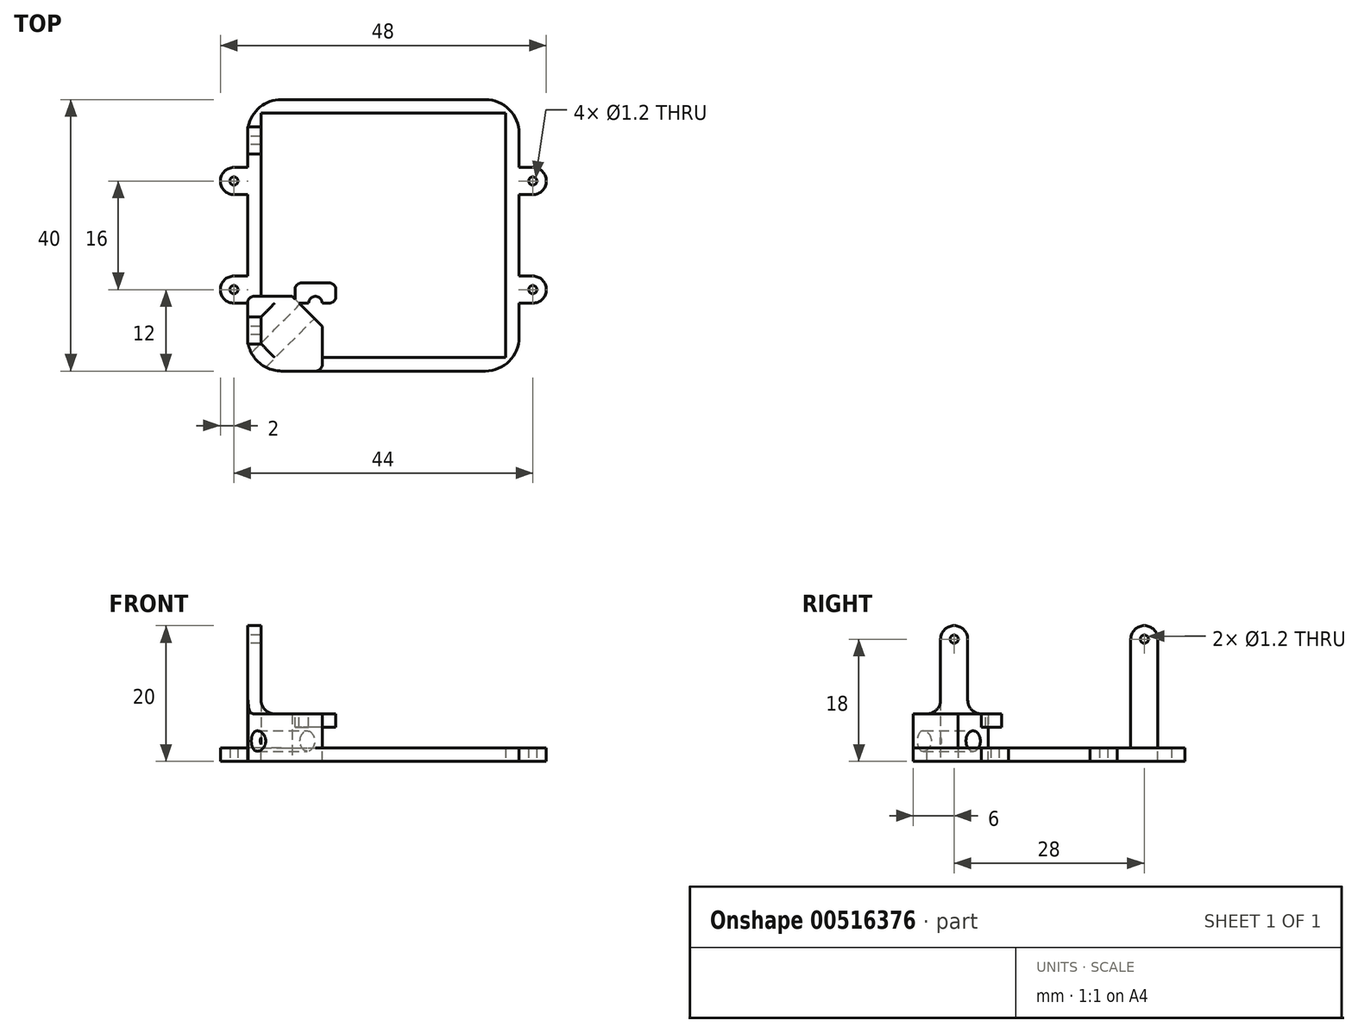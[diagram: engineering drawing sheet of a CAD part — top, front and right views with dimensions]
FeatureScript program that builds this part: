
annotation { "Feature Type Name" : "Feature", "Feature Type Description" : "" }
export const myFeature = defineFeature(function(context is Context, id is Id, definition is map)
    precondition{}
    {
        {
            var Q0;
            Q0=qCreatedBy(makeId("Top.planeOp"),FACE);
            var sketch = newSketch(context, id + "F0", { "sketchPlane" : qUnion([Q0])});
            skLineSegment(sketch, "E0.bottom", {"start": v(-10, 10) * mm, "end": v(10, 10) * mm, "construction": true});
            skLineSegment(sketch, "E0.top", {"start": v(-10, -10) * mm, "end": v(10, -10) * mm, "construction": true});
            skLineSegment(sketch, "E0.left", {"start": v(-10, 10) * mm, "end": v(-10, -10) * mm, "construction": true});
            skLineSegment(sketch, "E0.right", {"start": v(10, 10) * mm, "end": v(10, -10) * mm, "construction": true});
            skPoint(sketch, "E0.middle", {"position": v(0, 0) * mm});
            skCircle(sketch, "E1", {"center": v(-10, 10) * mm, "radius": 1 * mm});
            skCircle(sketch, "E2", {"center": v(-10, -10) * mm, "radius": 1 * mm});
            skCircle(sketch, "E3", {"center": v(10, -10) * mm, "radius": 1 * mm});
            skCircle(sketch, "E4", {"center": v(10, 10) * mm, "radius": 1 * mm});
            skLineSegment(sketch, "E5.bottom", {"start": v(-22, 8) * mm, "end": v(22, 8) * mm, "construction": true});
            skLineSegment(sketch, "E5.top", {"start": v(-22, -8) * mm, "end": v(22, -8) * mm, "construction": true});
            skLineSegment(sketch, "E5.left", {"start": v(-22, 8) * mm, "end": v(-22, -8) * mm, "construction": true});
            skLineSegment(sketch, "E5.right", {"start": v(22, 8) * mm, "end": v(22, -8) * mm, "construction": true});
            skCircle(sketch, "E6", {"center": v(-22, 8) * mm, "radius": 0.6 * mm});
            skCircle(sketch, "E7", {"center": v(22, 8) * mm, "radius": 0.6 * mm});
            skCircle(sketch, "E8", {"center": v(22, -8) * mm, "radius": 0.6 * mm});
            skCircle(sketch, "E9", {"center": v(-22, -8) * mm, "radius": 0.6 * mm});
            skLineSegment(sketch, "E10.bottom", {"start": v(-18, 18) * mm, "end": v(18, 18) * mm});
            skLineSegment(sketch, "E10.top", {"start": v(-18, -18) * mm, "end": v(18, -18) * mm});
            skLineSegment(sketch, "E10.left", {"start": v(-18, 18) * mm, "end": v(-18, -18) * mm});
            skLineSegment(sketch, "E10.right", {"start": v(18, 18) * mm, "end": v(18, -18) * mm});
            skLineSegment(sketch, "E11.bottom", {"start": v(-20, 20) * mm, "end": v(20, 20) * mm});
            skLineSegment(sketch, "E11.top", {"start": v(-20, -20) * mm, "end": v(20, -20) * mm});
            skLineSegment(sketch, "E11.left", {"start": v(-20, 20) * mm, "end": v(-20, -20) * mm});
            skLineSegment(sketch, "E11.right", {"start": v(20, 20) * mm, "end": v(20, -20) * mm});
            skArc(sketch, "E12", {"start": v(-22, 10) * mm, "mid": v(-24, 8) * mm, "end": v(-22, 6) * mm});
            skLineSegment(sketch, "E13.bottom", {"start": v(-22, 10) * mm, "end": v(22, 10) * mm});
            skLineSegment(sketch, "E13.top", {"start": v(-22, 6) * mm, "end": v(22, 6) * mm});
            skLineSegment(sketch, "E13.left", {"start": v(-22, 10) * mm, "end": v(-22, 6) * mm});
            skLineSegment(sketch, "E13.right", {"start": v(22, 10) * mm, "end": v(22, 6) * mm});
            skArc(sketch, "E14", {"start": v(22, 10) * mm, "mid": v(24, 8) * mm, "end": v(22, 6) * mm});
            skLineSegment(sketch, "E15.bottom", {"start": v(-22, -6) * mm, "end": v(22, -6) * mm});
            skLineSegment(sketch, "E15.top", {"start": v(-22, -10) * mm, "end": v(22, -10) * mm});
            skLineSegment(sketch, "E15.left", {"start": v(-22, -6) * mm, "end": v(-22, -10) * mm});
            skLineSegment(sketch, "E15.right", {"start": v(22, -6) * mm, "end": v(22, -10) * mm});
            skArc(sketch, "E16", {"start": v(-22, -6) * mm, "mid": v(-24, -8) * mm, "end": v(-22, -10) * mm});
            skArc(sketch, "E17", {"start": v(22, -6) * mm, "mid": v(24, -8) * mm, "end": v(22, -10) * mm});
            skLineSegment(sketch, "E18.bottom", {"start": v(-13.5, 13.5) * mm, "end": v(13.5, 13.5) * mm, "construction": true});
            skLineSegment(sketch, "E18.top", {"start": v(-13.5, -13.5) * mm, "end": v(13.5, -13.5) * mm, "construction": true});
            skLineSegment(sketch, "E18.left", {"start": v(-13.5, 13.5) * mm, "end": v(-13.5, -13.5) * mm, "construction": true});
            skLineSegment(sketch, "E18.right", {"start": v(13.5, 13.5) * mm, "end": v(13.5, -13.5) * mm, "construction": true});
            skLineSegment(sketch, "E19.bottom", {"start": v(-7, 7) * mm, "end": v(7, 7) * mm, "construction": true});
            skLineSegment(sketch, "E19.top", {"start": v(-7, -7) * mm, "end": v(7, -7) * mm, "construction": true});
            skLineSegment(sketch, "E19.left", {"start": v(-7, 7) * mm, "end": v(-7, -7) * mm, "construction": true});
            skLineSegment(sketch, "E19.right", {"start": v(7, 7) * mm, "end": v(7, -7) * mm, "construction": true});
            skSolve(sketch);
        }
        {
            var Q0;
            Q0 = qSketchRegion(id + "F0", true);
            extrude(context, id + "F1", {"entities" : qUnion([Q0]), "depth" : 2 * mm, "offsetDistance" : 25 * mm});
        }
        {
            var Q0;
            Q0=qCreatedBy(makeId("Top.planeOp"),FACE);
            var sketch = newSketch(context, id + "F2", { "sketchPlane" : qUnion([Q0])});
            skLineSegment(sketch, "E20.0", {"start": v(-20, -20) * mm, "end": v(20, -20) * mm});
            skLineSegment(sketch, "E20.1", {"start": v(-20, 20) * mm, "end": v(-20, -20) * mm});
            skLineSegment(sketch, "E21", {"start": v(-20, -2.4) * mm, "end": v(-2.4, -20) * mm});
            skLineSegment(sketch, "E22.bottom", {"start": v(-20, -20) * mm, "end": v(-8.99, -20) * mm});
            skLineSegment(sketch, "E22.top", {"start": v(-20, -8.99) * mm, "end": v(-8.99, -8.99) * mm});
            skLineSegment(sketch, "E22.left", {"start": v(-20, -20) * mm, "end": v(-20, -8.99) * mm});
            skLineSegment(sketch, "E22.right", {"start": v(-8.99, -20) * mm, "end": v(-8.99, -8.99) * mm});
            skSolve(sketch);
        }
        {
            var Q0;
            {var subQ0=sQuery(id+"F2.wireOp",EDGE,"E22.right");var subQ7=sQuery(id+"F2.wireOp",EDGE,"E20.0");var subQ9=makeQuery(id+"F2.imprint","INTERSECT",VERTEX,{"derivedFrom":[subQ7,subQ0]});Q0=makeQuery(id+"F2.imprint","IMPRINT",FACE,{"disambiguationData":[TD([[makeQuery(id+"F2.imprint","IMPRINT",EDGE,{"disambiguationData":[TD([[subQ9,1.0]])],"derivedFrom":subQ7}),1.0]])]});}
            extrude(context, id + "F3", {"entities" : qUnion([Q0]), "operationType" : NewBodyOperationType.ADD, "depth" : 7 * mm, "offsetDistance" : 25 * mm});
        }
        {
            var Q0;
            Q0=makeQuery(id+"F3.opExtrude","SWEPT_FACE",FACE,{"disambiguationData":[OSD([sQuery(id+"F2.wireOp",EDGE,"E21")])]});
            var sketch = newSketch(context, id + "F4", { "sketchPlane" : qUnion([Q0])});
            skCircle(sketch, "E23", {"center": v(0, 3) * mm, "radius": 1.5 * mm});
            skSolve(sketch);
        }
        {
            var Q0;
            Q0 = qSketchRegion(id + "F4", true);
            extrude(context, id + "F5", {"entities" : qUnion([Q0]), "operationType" : NewBodyOperationType.REMOVE, "oppositeDirection" : true, "depth" : 25 * mm, "offsetDistance" : 25 * mm});
        }
        {
            var Q0;
            Q0=makeQuery(id+"F3.opExtrude","CAP_FACE",FACE,{"disambiguationData":[OSD([sQuery(id+"F2.wireOp",EDGE,"E20.0"),sQuery(id+"F2.wireOp",EDGE,"E20.1"),sQuery(id+"F2.wireOp",EDGE,"E21"),sQuery(id+"F2.wireOp",EDGE,"E22.top"),sQuery(id+"F2.wireOp",EDGE,"E22.right")])],"isStart":false});
            var sketch = newSketch(context, id + "F6", { "sketchPlane" : qUnion([Q0])});
            skLineSegment(sketch, "E24.0", {"start": v(-10, 10) * mm, "end": v(10, 10) * mm});
            skLineSegment(sketch, "E24.1", {"start": v(-10, -10) * mm, "end": v(10, -10) * mm});
            skLineSegment(sketch, "E24.2", {"start": v(-10, 10) * mm, "end": v(-10, -10) * mm});
            skLineSegment(sketch, "E24.3", {"start": v(10, 10) * mm, "end": v(10, -10) * mm});
            skPoint(sketch, "E24.4", {"position": v(0, 0) * mm});
            skCircle(sketch, "E24.5", {"center": v(-10, 10) * mm, "radius": 1 * mm});
            skCircle(sketch, "E24.6", {"center": v(-10, -10) * mm, "radius": 1 * mm});
            skCircle(sketch, "E24.7", {"center": v(10, -10) * mm, "radius": 1 * mm});
            skCircle(sketch, "E24.8", {"center": v(10, 10) * mm, "radius": 1 * mm});
            skLineSegment(sketch, "E24.9", {"start": v(-22, 8) * mm, "end": v(22, 8) * mm});
            skLineSegment(sketch, "E24.10", {"start": v(-22, -8) * mm, "end": v(22, -8) * mm});
            skLineSegment(sketch, "E24.11", {"start": v(-22, 8) * mm, "end": v(-22, -8) * mm});
            skLineSegment(sketch, "E24.12", {"start": v(22, 8) * mm, "end": v(22, -8) * mm});
            skPoint(sketch, "E24.13", {"position": v(0, 0) * mm});
            skCircle(sketch, "E24.14", {"center": v(-22, 8) * mm, "radius": 0.6 * mm});
            skCircle(sketch, "E24.15", {"center": v(22, 8) * mm, "radius": 0.6 * mm});
            skCircle(sketch, "E24.16", {"center": v(22, -8) * mm, "radius": 0.6 * mm});
            skCircle(sketch, "E24.17", {"center": v(-22, -8) * mm, "radius": 0.6 * mm});
            skLineSegment(sketch, "E24.18", {"start": v(-18, 18) * mm, "end": v(18, 18) * mm});
            skLineSegment(sketch, "E24.19", {"start": v(-18, -18) * mm, "end": v(18, -18) * mm});
            skLineSegment(sketch, "E24.20", {"start": v(-18, 18) * mm, "end": v(-18, -18) * mm});
            skLineSegment(sketch, "E24.21", {"start": v(18, 18) * mm, "end": v(18, -18) * mm});
            skPoint(sketch, "E24.22", {"position": v(0, 0) * mm});
            skLineSegment(sketch, "E24.23", {"start": v(-20, 20) * mm, "end": v(20, 20) * mm});
            skLineSegment(sketch, "E24.24", {"start": v(-20, -20) * mm, "end": v(20, -20) * mm});
            skLineSegment(sketch, "E24.25", {"start": v(-20, 20) * mm, "end": v(-20, -20) * mm});
            skLineSegment(sketch, "E24.26", {"start": v(20, 20) * mm, "end": v(20, -20) * mm});
            skPoint(sketch, "E24.27", {"position": v(0, 0) * mm});
            skArc(sketch, "E24.28", {"start": v(-22, 10) * mm, "mid": v(-24, 8) * mm, "end": v(-22, 6) * mm});
            skLineSegment(sketch, "E24.29", {"start": v(-22, 10) * mm, "end": v(22, 10) * mm});
            skLineSegment(sketch, "E24.30", {"start": v(-22, 6) * mm, "end": v(22, 6) * mm});
            skLineSegment(sketch, "E24.31", {"start": v(-22, 10) * mm, "end": v(-22, 6) * mm});
            skLineSegment(sketch, "E24.32", {"start": v(22, 10) * mm, "end": v(22, 6) * mm});
            skArc(sketch, "E24.33", {"start": v(22, 10) * mm, "mid": v(24, 8) * mm, "end": v(22, 6) * mm});
            skLineSegment(sketch, "E24.34", {"start": v(-22, -6) * mm, "end": v(22, -6) * mm});
            skLineSegment(sketch, "E24.35", {"start": v(-22, -10) * mm, "end": v(22, -10) * mm});
            skLineSegment(sketch, "E24.36", {"start": v(-22, -6) * mm, "end": v(-22, -10) * mm});
            skLineSegment(sketch, "E24.37", {"start": v(22, -6) * mm, "end": v(22, -10) * mm});
            skArc(sketch, "E24.38", {"start": v(-22, -6) * mm, "mid": v(-24, -8) * mm, "end": v(-22, -10) * mm});
            skArc(sketch, "E24.39", {"start": v(22, -6) * mm, "mid": v(24, -8) * mm, "end": v(22, -10) * mm});
            skLineSegment(sketch, "E24.40", {"start": v(-13.5, 13.5) * mm, "end": v(13.5, 13.5) * mm});
            skLineSegment(sketch, "E24.41", {"start": v(-13.5, -13.5) * mm, "end": v(13.5, -13.5) * mm});
            skLineSegment(sketch, "E24.42", {"start": v(-13.5, 13.5) * mm, "end": v(-13.5, -13.5) * mm});
            skLineSegment(sketch, "E24.43", {"start": v(13.5, 13.5) * mm, "end": v(13.5, -13.5) * mm});
            skPoint(sketch, "E24.44", {"position": v(0, 0) * mm});
            skLineSegment(sketch, "E24.45", {"start": v(-7, 7) * mm, "end": v(7, 7) * mm});
            skLineSegment(sketch, "E24.46", {"start": v(-7, -7) * mm, "end": v(7, -7) * mm});
            skLineSegment(sketch, "E24.47", {"start": v(-7, 7) * mm, "end": v(-7, -7) * mm});
            skLineSegment(sketch, "E24.48", {"start": v(7, 7) * mm, "end": v(7, -7) * mm});
            skPoint(sketch, "E24.49", {"position": v(0, 0) * mm});
            skLineSegment(sketch, "E25.bottom", {"start": v(-7, -7) * mm, "end": v(-13, -7) * mm});
            skLineSegment(sketch, "E25.top", {"start": v(-7, -13) * mm, "end": v(-13, -13) * mm});
            skLineSegment(sketch, "E25.left", {"start": v(-7, -7) * mm, "end": v(-7, -13) * mm});
            skLineSegment(sketch, "E25.right", {"start": v(-13, -7) * mm, "end": v(-13, -13) * mm});
            skSolve(sketch);
        }
        {
            var Q0;
            {var subQ5=sQuery(id+"F6.wireOp",EDGE,"E24.10");var subQ6=sQuery(id+"F6.wireOp",EDGE,"E24.2");var subQ7=makeQuery(id+"F6.imprint","INTERSECT",VERTEX,{"derivedFrom":[subQ6,subQ5]});Q0=makeQuery(id+"F6.imprint","IMPRINT",FACE,{"disambiguationData":[TD([[makeQuery(id+"F6.imprint","IMPRINT",EDGE,{"disambiguationData":[TD([[subQ7,-1.0]])],"derivedFrom":subQ6}),1.0]])]});}
            var Q1;
            {var subQ0=sQuery(id+"F6.wireOp",EDGE,"E25.bottom");var subQ1=sQuery(id+"F6.wireOp",EDGE,"E24.2");var subQ2=makeQuery(id+"F6.imprint","INTERSECT",VERTEX,{"derivedFrom":[subQ1,subQ0]});Q1=makeQuery(id+"F6.imprint","IMPRINT",FACE,{"disambiguationData":[TD([[makeQuery(id+"F6.imprint","IMPRINT",EDGE,{"disambiguationData":[TD([[subQ2,-1.0]])],"derivedFrom":subQ1}),1.0]])]});}
            var Q2;
            {var subQ0=sQuery(id+"F6.wireOp",EDGE,"E25.bottom");var subQ1=sQuery(id+"F6.wireOp",EDGE,"E24.2");var subQ2=makeQuery(id+"F6.imprint","INTERSECT",VERTEX,{"derivedFrom":[subQ1,subQ0]});Q2=makeQuery(id+"F6.imprint","IMPRINT",FACE,{"disambiguationData":[TD([[makeQuery(id+"F6.imprint","IMPRINT",EDGE,{"disambiguationData":[TD([[subQ2,-1.0]])],"derivedFrom":subQ1}),-1.0]])]});}
            var Q3;
            {var subQ0=sQuery(id+"F6.wireOp",EDGE,"E24.10");var subQ1=sQuery(id+"F6.wireOp",EDGE,"E24.2");var subQ2=makeQuery(id+"F6.imprint","INTERSECT",VERTEX,{"derivedFrom":[subQ1,subQ0]});Q3=makeQuery(id+"F6.imprint","IMPRINT",FACE,{"disambiguationData":[TD([[makeQuery(id+"F6.imprint","IMPRINT",EDGE,{"disambiguationData":[TD([[subQ2,-1.0]])],"derivedFrom":subQ1}),-1.0]])]});}
            var Q4;
            {var subQ0=sQuery(id+"F6.wireOp",EDGE,"E25.right");var subQ1=sQuery(id+"F6.wireOp",EDGE,"E24.35");var subQ2=makeQuery(id+"F6.imprint","INTERSECT",VERTEX,{"derivedFrom":[subQ1,subQ0]});Q4=makeQuery(id+"F6.imprint","IMPRINT",FACE,{"disambiguationData":[TD([[makeQuery(id+"F6.imprint","IMPRINT",EDGE,{"disambiguationData":[TD([[subQ2,-1.0]])],"derivedFrom":subQ1}),-1.0]])]});}
            var Q5;
            {var subQ0=sQuery(id+"F6.wireOp",EDGE,"E24.35");var subQ1=sQuery(id+"F6.wireOp",EDGE,"E24.6");var subQ2=makeQuery(id+"F6.imprint","INTERSECT",VERTEX,{"disambiguationData":[OD(0.0)],"derivedFrom":[subQ1,subQ0]});Q5=makeQuery(id+"F6.imprint","IMPRINT",FACE,{"disambiguationData":[TD([[makeQuery(id+"F6.imprint","IMPRINT",EDGE,{"disambiguationData":[TD([[subQ2,1.0]])],"derivedFrom":subQ1}),-1.0]])]});}
            extrude(context, id + "F7", {"entities" : qUnion([Q0, Q1, Q2, Q3, Q4, Q5]), "operationType" : NewBodyOperationType.ADD, "oppositeDirection" : true, "depth" : 2 * mm, "offsetDistance" : 25 * mm});
        }
        {
            var Q0;
            {var subQ0=sQuery(id+"F2.wireOp",EDGE,"E20.1");var subQ1=sQuery(id+"F2.wireOp",EDGE,"E20.0");var subQ2=sQuery(id+"F0.wireOp",EDGE,"E11.left");var subQ3=sQuery(id+"F0.wireOp",EDGE,"E11.top");Q0=makeQuery(id+"F5.boolean.opBoolean","SPLIT",EDGE,{"disambiguationData":[TD([makeQuery(id+"F3.opExtrude","CAP_FACE",FACE,{"disambiguationData":[OSD([subQ1,subQ0,sQuery(id+"F2.wireOp",EDGE,"E21"),sQuery(id+"F2.wireOp",EDGE,"E22.top"),sQuery(id+"F2.wireOp",EDGE,"E22.right")])],"isStart":false})])],"derivedFrom":makeQuery(id+"F3.boolean.opBoolean","MERGE",EDGE,{"derivedFrom":[makeQuery(id+"F1.opExtrude","SWEPT_EDGE",EDGE,{"disambiguationData":[OSD([subQ3,subQ2])]}),makeQuery(id+"F3.opExtrude","SWEPT_EDGE",EDGE,{"disambiguationData":[OSD([subQ1,subQ0])]})]})});}
            var Q1;
            {var subQ0=sQuery(id+"F2.wireOp",EDGE,"E20.0");var subQ1=sQuery(id+"F0.wireOp",EDGE,"E11.right");var subQ2=sQuery(id+"F0.wireOp",EDGE,"E11.top");var subQ3=sQuery(id+"F2.wireOp",EDGE,"E20.1");Q1=makeQuery(id+"F495DjvZ0ecShgZ_1.1.F5.boolean.opBoolean","SPLIT",EDGE,{"disambiguationData":[TD([makeQuery(id+"F495DjvZ0ecShgZ_1.1.F3.opExtrude","CAP_FACE",FACE,{"disambiguationData":[OSD([subQ0,subQ3,sQuery(id+"F2.wireOp",EDGE,"E21"),sQuery(id+"F2.wireOp",EDGE,"E22.top"),sQuery(id+"F2.wireOp",EDGE,"E22.right")])],"isStart":false})])],"derivedFrom":makeQuery(id+"F495DjvZ0ecShgZ_1.1.F3.boolean.opBoolean","MERGE",EDGE,{"derivedFrom":[makeQuery(id+"F1.opExtrude","SWEPT_EDGE",EDGE,{"disambiguationData":[OSD([subQ2,subQ1])]}),makeQuery(id+"F495DjvZ0ecShgZ_1.1.F3.opExtrude","SWEPT_EDGE",EDGE,{"disambiguationData":[OSD([subQ0,subQ3])]})]})});}
            var Q2;
            {var subQ0=sQuery(id+"F2.wireOp",EDGE,"E20.1");var subQ1=sQuery(id+"F2.wireOp",EDGE,"E20.0");var subQ2=sQuery(id+"F0.wireOp",EDGE,"E11.bottom");var subQ3=sQuery(id+"F0.wireOp",EDGE,"E11.right");Q2=makeQuery(id+"FbS9UsEZToCQNxt_1.1.F495DjvZ0ecShgZ_1.1.F5.boolean.opBoolean","SPLIT",EDGE,{"disambiguationData":[TD([makeQuery(id+"FbS9UsEZToCQNxt_1.1.F495DjvZ0ecShgZ_1.1.F3.opExtrude","CAP_FACE",FACE,{"disambiguationData":[OSD([subQ1,subQ0,sQuery(id+"F2.wireOp",EDGE,"E21"),sQuery(id+"F2.wireOp",EDGE,"E22.top"),sQuery(id+"F2.wireOp",EDGE,"E22.right")])],"isStart":false})])],"derivedFrom":makeQuery(id+"FbS9UsEZToCQNxt_1.1.F495DjvZ0ecShgZ_1.1.F3.boolean.opBoolean","MERGE",EDGE,{"derivedFrom":[makeQuery(id+"F1.opExtrude","SWEPT_EDGE",EDGE,{"disambiguationData":[OSD([subQ2,subQ3])]}),makeQuery(id+"FbS9UsEZToCQNxt_1.1.F495DjvZ0ecShgZ_1.1.F3.opExtrude","SWEPT_EDGE",EDGE,{"disambiguationData":[OSD([subQ1,subQ0])]})]})});}
            var Q3;
            {var subQ0=sQuery(id+"F2.wireOp",EDGE,"E20.0");var subQ1=sQuery(id+"F0.wireOp",EDGE,"E11.bottom");var subQ2=sQuery(id+"F0.wireOp",EDGE,"E11.left");var subQ3=sQuery(id+"F2.wireOp",EDGE,"E20.1");Q3=makeQuery(id+"F3mywzViK7ot0tf_1.1.FbS9UsEZToCQNxt_1.1.F495DjvZ0ecShgZ_1.1.F5.boolean.opBoolean","SPLIT",EDGE,{"disambiguationData":[TD([makeQuery(id+"F3mywzViK7ot0tf_1.1.FbS9UsEZToCQNxt_1.1.F495DjvZ0ecShgZ_1.1.F3.opExtrude","CAP_FACE",FACE,{"disambiguationData":[OSD([subQ0,subQ3,sQuery(id+"F2.wireOp",EDGE,"E21"),sQuery(id+"F2.wireOp",EDGE,"E22.top"),sQuery(id+"F2.wireOp",EDGE,"E22.right")])],"isStart":false})])],"derivedFrom":makeQuery(id+"F3mywzViK7ot0tf_1.1.FbS9UsEZToCQNxt_1.1.F495DjvZ0ecShgZ_1.1.F3.boolean.opBoolean","MERGE",EDGE,{"derivedFrom":[makeQuery(id+"F1.opExtrude","SWEPT_EDGE",EDGE,{"disambiguationData":[OSD([subQ1,subQ2])]}),makeQuery(id+"F3mywzViK7ot0tf_1.1.FbS9UsEZToCQNxt_1.1.F495DjvZ0ecShgZ_1.1.F3.opExtrude","SWEPT_EDGE",EDGE,{"disambiguationData":[OSD([subQ0,subQ3])]})]})});}
            var Q4;
            Q4=makeQuery(id+"F7.opExtrude","SWEPT_EDGE",EDGE,{"disambiguationData":[OSD([sQuery(id+"F2.wireOp",EDGE,"E21"),sQuery(id+"F6.wireOp",EDGE,"E25.right")])]});
            var Q5;
            Q5=makeQuery(id+"F7.boolean.opBoolean","INTERSECT",EDGE,{"derivedFrom":[makeQuery(id+"F3.opExtrude","SWEPT_FACE",FACE,{"disambiguationData":[OSD([sQuery(id+"F2.wireOp",EDGE,"E21")])]}),makeQuery(id+"F7.opExtrude","SWEPT_FACE",FACE,{"disambiguationData":[OSD([sQuery(id+"F6.wireOp",EDGE,"E25.top")])]})]});
            var Q6;
            Q6=makeQuery(id+"F495DjvZ0ecShgZ_1.1.F7.boolean.opBoolean","INTERSECT",EDGE,{"derivedFrom":[makeQuery(id+"F495DjvZ0ecShgZ_1.1.F3.opExtrude","SWEPT_FACE",FACE,{"disambiguationData":[OSD([sQuery(id+"F2.wireOp",EDGE,"E21")])]}),makeQuery(id+"F495DjvZ0ecShgZ_1.1.F7.opExtrude","SWEPT_FACE",FACE,{"disambiguationData":[OSD([sQuery(id+"F6.wireOp",EDGE,"E25.top")])]})]});
            var Q7;
            Q7=makeQuery(id+"F495DjvZ0ecShgZ_1.1.F7.opExtrude","SWEPT_EDGE",EDGE,{"disambiguationData":[OSD([sQuery(id+"F2.wireOp",EDGE,"E21"),sQuery(id+"F6.wireOp",EDGE,"E25.right")])]});
            var Q8;
            Q8=makeQuery(id+"FbS9UsEZToCQNxt_1.1.F495DjvZ0ecShgZ_1.1.F7.opExtrude","SWEPT_EDGE",EDGE,{"disambiguationData":[OSD([sQuery(id+"F2.wireOp",EDGE,"E21"),sQuery(id+"F6.wireOp",EDGE,"E25.right")])]});
            var Q9;
            Q9=makeQuery(id+"FbS9UsEZToCQNxt_1.1.F495DjvZ0ecShgZ_1.1.F7.boolean.opBoolean","INTERSECT",EDGE,{"derivedFrom":[makeQuery(id+"FbS9UsEZToCQNxt_1.1.F495DjvZ0ecShgZ_1.1.F3.opExtrude","SWEPT_FACE",FACE,{"disambiguationData":[OSD([sQuery(id+"F2.wireOp",EDGE,"E21")])]}),makeQuery(id+"FbS9UsEZToCQNxt_1.1.F495DjvZ0ecShgZ_1.1.F7.opExtrude","SWEPT_FACE",FACE,{"disambiguationData":[OSD([sQuery(id+"F6.wireOp",EDGE,"E25.top")])]})]});
            var Q10;
            Q10=makeQuery(id+"F3mywzViK7ot0tf_1.1.FbS9UsEZToCQNxt_1.1.F495DjvZ0ecShgZ_1.1.F7.boolean.opBoolean","INTERSECT",EDGE,{"derivedFrom":[makeQuery(id+"F3mywzViK7ot0tf_1.1.FbS9UsEZToCQNxt_1.1.F495DjvZ0ecShgZ_1.1.F3.opExtrude","SWEPT_FACE",FACE,{"disambiguationData":[OSD([sQuery(id+"F2.wireOp",EDGE,"E21")])]}),makeQuery(id+"F3mywzViK7ot0tf_1.1.FbS9UsEZToCQNxt_1.1.F495DjvZ0ecShgZ_1.1.F7.opExtrude","SWEPT_FACE",FACE,{"disambiguationData":[OSD([sQuery(id+"F6.wireOp",EDGE,"E25.top")])]})]});
            var Q11;
            Q11=makeQuery(id+"F3mywzViK7ot0tf_1.1.FbS9UsEZToCQNxt_1.1.F495DjvZ0ecShgZ_1.1.F7.opExtrude","SWEPT_EDGE",EDGE,{"disambiguationData":[OSD([sQuery(id+"F2.wireOp",EDGE,"E21"),sQuery(id+"F6.wireOp",EDGE,"E25.right")])]});
            fillet(context, id + "F8", {"entities" : qUnion([Q0, Q1, Q2, Q3, Q4, Q5, Q6, Q7, Q8, Q9, Q10, Q11]), "radius" : 5 * mm, "tangentPropagation" : true, "allowEdgeOverflow" : false});
        }
        {
            var Q0;
            Q0=makeQuery(id+"FbS9UsEZToCQNxt_1.1.F495DjvZ0ecShgZ_1.1.F7.opExtrude","SWEPT_EDGE",EDGE,{"disambiguationData":[OSD([sQuery(id+"F6.wireOp",EDGE,"E24.46"),sQuery(id+"F6.wireOp",EDGE,"E24.47"),sQuery(id+"F6.wireOp",EDGE,"E25.bottom"),sQuery(id+"F6.wireOp",EDGE,"E25.left")])]});
            var Q1;
            Q1=makeQuery(id+"FbS9UsEZToCQNxt_1.1.F495DjvZ0ecShgZ_1.1.F7.opExtrude","SWEPT_EDGE",EDGE,{"disambiguationData":[OSD([sQuery(id+"F6.wireOp",EDGE,"E25.bottom"),sQuery(id+"F6.wireOp",EDGE,"E25.right")])]});
            var Q2;
            Q2=makeQuery(id+"FbS9UsEZToCQNxt_1.1.F495DjvZ0ecShgZ_1.1.F7.opExtrude","SWEPT_EDGE",EDGE,{"disambiguationData":[OSD([sQuery(id+"F6.wireOp",EDGE,"E25.top"),sQuery(id+"F6.wireOp",EDGE,"E25.left")])]});
            var Q3;
            Q3=makeQuery(id+"F8.opFillet","BLEND_EDGE",EDGE,{"blendedFrom":[makeQuery(id+"FbS9UsEZToCQNxt_1.1.F495DjvZ0ecShgZ_1.1.F7.boolean.opBoolean","INTERSECT",EDGE,{"derivedFrom":[makeQuery(id+"FbS9UsEZToCQNxt_1.1.F495DjvZ0ecShgZ_1.1.F3.opExtrude","SWEPT_FACE",FACE,{"disambiguationData":[OSD([sQuery(id+"F2.wireOp",EDGE,"E21")])]}),makeQuery(id+"FbS9UsEZToCQNxt_1.1.F495DjvZ0ecShgZ_1.1.F7.opExtrude","SWEPT_FACE",FACE,{"disambiguationData":[OSD([sQuery(id+"F6.wireOp",EDGE,"E25.top")])]})]}),makeQuery(id+"FbS9UsEZToCQNxt_1.1.F495DjvZ0ecShgZ_1.1.F3.opExtrude","SWEPT_FACE",FACE,{"disambiguationData":[OSD([sQuery(id+"F2.wireOp",EDGE,"E22.right")])]})],"blendedInto":[makeQuery(id+"FbS9UsEZToCQNxt_1.1.F495DjvZ0ecShgZ_1.1.F3.opExtrude","SWEPT_FACE",FACE,{"disambiguationData":[OSD([sQuery(id+"F2.wireOp",EDGE,"E22.right")])]})]});
            var Q4;
            Q4=makeQuery(id+"F8.opFillet","BLEND_EDGE",EDGE,{"blendedFrom":[makeQuery(id+"FbS9UsEZToCQNxt_1.1.F495DjvZ0ecShgZ_1.1.F7.opExtrude","SWEPT_EDGE",EDGE,{"disambiguationData":[OSD([sQuery(id+"F2.wireOp",EDGE,"E21"),sQuery(id+"F6.wireOp",EDGE,"E25.right")])]}),makeQuery(id+"FbS9UsEZToCQNxt_1.1.F495DjvZ0ecShgZ_1.1.F3.opExtrude","SWEPT_FACE",FACE,{"disambiguationData":[OSD([sQuery(id+"F2.wireOp",EDGE,"E22.top")])]})],"blendedInto":[makeQuery(id+"FbS9UsEZToCQNxt_1.1.F495DjvZ0ecShgZ_1.1.F3.opExtrude","SWEPT_FACE",FACE,{"disambiguationData":[OSD([sQuery(id+"F2.wireOp",EDGE,"E22.top")])]})]});
            var Q5;
            Q5=makeQuery(id+"FbS9UsEZToCQNxt_1.1.F495DjvZ0ecShgZ_1.1.F3.opExtrude","SWEPT_EDGE",EDGE,{"disambiguationData":[OSD([sQuery(id+"F2.wireOp",EDGE,"E20.1"),sQuery(id+"F2.wireOp",EDGE,"E22.top")])]});
            var Q6;
            Q6=makeQuery(id+"FbS9UsEZToCQNxt_1.1.F495DjvZ0ecShgZ_1.1.F3.opExtrude","SWEPT_EDGE",EDGE,{"disambiguationData":[OSD([sQuery(id+"F2.wireOp",EDGE,"E20.0"),sQuery(id+"F2.wireOp",EDGE,"E22.right")])]});
            var Q7;
            Q7=makeQuery(id+"F3mywzViK7ot0tf_1.1.FbS9UsEZToCQNxt_1.1.F495DjvZ0ecShgZ_1.1.F3.opExtrude","SWEPT_EDGE",EDGE,{"disambiguationData":[OSD([sQuery(id+"F2.wireOp",EDGE,"E20.0"),sQuery(id+"F2.wireOp",EDGE,"E22.right")])]});
            var Q8;
            Q8=makeQuery(id+"F8.opFillet","BLEND_EDGE",EDGE,{"blendedFrom":[makeQuery(id+"F3mywzViK7ot0tf_1.1.FbS9UsEZToCQNxt_1.1.F495DjvZ0ecShgZ_1.1.F7.boolean.opBoolean","INTERSECT",EDGE,{"derivedFrom":[makeQuery(id+"F3mywzViK7ot0tf_1.1.FbS9UsEZToCQNxt_1.1.F495DjvZ0ecShgZ_1.1.F3.opExtrude","SWEPT_FACE",FACE,{"disambiguationData":[OSD([sQuery(id+"F2.wireOp",EDGE,"E21")])]}),makeQuery(id+"F3mywzViK7ot0tf_1.1.FbS9UsEZToCQNxt_1.1.F495DjvZ0ecShgZ_1.1.F7.opExtrude","SWEPT_FACE",FACE,{"disambiguationData":[OSD([sQuery(id+"F6.wireOp",EDGE,"E25.top")])]})]}),makeQuery(id+"F3mywzViK7ot0tf_1.1.FbS9UsEZToCQNxt_1.1.F495DjvZ0ecShgZ_1.1.F3.opExtrude","SWEPT_FACE",FACE,{"disambiguationData":[OSD([sQuery(id+"F2.wireOp",EDGE,"E22.right")])]})],"blendedInto":[makeQuery(id+"F3mywzViK7ot0tf_1.1.FbS9UsEZToCQNxt_1.1.F495DjvZ0ecShgZ_1.1.F3.opExtrude","SWEPT_FACE",FACE,{"disambiguationData":[OSD([sQuery(id+"F2.wireOp",EDGE,"E22.right")])]})]});
            var Q9;
            Q9=makeQuery(id+"F3mywzViK7ot0tf_1.1.FbS9UsEZToCQNxt_1.1.F495DjvZ0ecShgZ_1.1.F7.opExtrude","SWEPT_EDGE",EDGE,{"disambiguationData":[OSD([sQuery(id+"F6.wireOp",EDGE,"E25.top"),sQuery(id+"F6.wireOp",EDGE,"E25.left")])]});
            var Q10;
            Q10=makeQuery(id+"F3mywzViK7ot0tf_1.1.FbS9UsEZToCQNxt_1.1.F495DjvZ0ecShgZ_1.1.F7.opExtrude","SWEPT_EDGE",EDGE,{"disambiguationData":[OSD([sQuery(id+"F6.wireOp",EDGE,"E24.46"),sQuery(id+"F6.wireOp",EDGE,"E24.47"),sQuery(id+"F6.wireOp",EDGE,"E25.bottom"),sQuery(id+"F6.wireOp",EDGE,"E25.left")])]});
            var Q11;
            Q11=makeQuery(id+"F3mywzViK7ot0tf_1.1.FbS9UsEZToCQNxt_1.1.F495DjvZ0ecShgZ_1.1.F7.opExtrude","SWEPT_EDGE",EDGE,{"disambiguationData":[OSD([sQuery(id+"F6.wireOp",EDGE,"E25.bottom"),sQuery(id+"F6.wireOp",EDGE,"E25.right")])]});
            var Q12;
            Q12=makeQuery(id+"F8.opFillet","BLEND_EDGE",EDGE,{"blendedFrom":[makeQuery(id+"F3mywzViK7ot0tf_1.1.FbS9UsEZToCQNxt_1.1.F495DjvZ0ecShgZ_1.1.F7.opExtrude","SWEPT_EDGE",EDGE,{"disambiguationData":[OSD([sQuery(id+"F2.wireOp",EDGE,"E21"),sQuery(id+"F6.wireOp",EDGE,"E25.right")])]}),makeQuery(id+"F3mywzViK7ot0tf_1.1.FbS9UsEZToCQNxt_1.1.F495DjvZ0ecShgZ_1.1.F3.opExtrude","SWEPT_FACE",FACE,{"disambiguationData":[OSD([sQuery(id+"F2.wireOp",EDGE,"E22.top")])]})],"blendedInto":[makeQuery(id+"F3mywzViK7ot0tf_1.1.FbS9UsEZToCQNxt_1.1.F495DjvZ0ecShgZ_1.1.F3.opExtrude","SWEPT_FACE",FACE,{"disambiguationData":[OSD([sQuery(id+"F2.wireOp",EDGE,"E22.top")])]})]});
            var Q13;
            Q13=makeQuery(id+"F3mywzViK7ot0tf_1.1.FbS9UsEZToCQNxt_1.1.F495DjvZ0ecShgZ_1.1.F3.opExtrude","SWEPT_EDGE",EDGE,{"disambiguationData":[OSD([sQuery(id+"F2.wireOp",EDGE,"E20.1"),sQuery(id+"F2.wireOp",EDGE,"E22.top")])]});
            var Q14;
            Q14=makeQuery(id+"F3.opExtrude","SWEPT_EDGE",EDGE,{"disambiguationData":[OSD([sQuery(id+"F2.wireOp",EDGE,"E20.1"),sQuery(id+"F2.wireOp",EDGE,"E22.top")])]});
            var Q15;
            Q15=makeQuery(id+"F8.opFillet","BLEND_EDGE",EDGE,{"blendedFrom":[makeQuery(id+"F7.opExtrude","SWEPT_EDGE",EDGE,{"disambiguationData":[OSD([sQuery(id+"F2.wireOp",EDGE,"E21"),sQuery(id+"F6.wireOp",EDGE,"E25.right")])]}),makeQuery(id+"F3.opExtrude","SWEPT_FACE",FACE,{"disambiguationData":[OSD([sQuery(id+"F2.wireOp",EDGE,"E22.top")])]})],"blendedInto":[makeQuery(id+"F3.opExtrude","SWEPT_FACE",FACE,{"disambiguationData":[OSD([sQuery(id+"F2.wireOp",EDGE,"E22.top")])]})]});
            var Q16;
            Q16=makeQuery(id+"F7.opExtrude","SWEPT_EDGE",EDGE,{"disambiguationData":[OSD([sQuery(id+"F6.wireOp",EDGE,"E25.bottom"),sQuery(id+"F6.wireOp",EDGE,"E25.right")])]});
            var Q17;
            Q17=makeQuery(id+"F7.opExtrude","SWEPT_EDGE",EDGE,{"disambiguationData":[OSD([sQuery(id+"F6.wireOp",EDGE,"E24.46"),sQuery(id+"F6.wireOp",EDGE,"E24.47"),sQuery(id+"F6.wireOp",EDGE,"E25.bottom"),sQuery(id+"F6.wireOp",EDGE,"E25.left")])]});
            var Q18;
            Q18=makeQuery(id+"F7.opExtrude","SWEPT_EDGE",EDGE,{"disambiguationData":[OSD([sQuery(id+"F6.wireOp",EDGE,"E25.top"),sQuery(id+"F6.wireOp",EDGE,"E25.left")])]});
            var Q19;
            Q19=makeQuery(id+"F8.opFillet","BLEND_EDGE",EDGE,{"blendedFrom":[makeQuery(id+"F7.boolean.opBoolean","INTERSECT",EDGE,{"derivedFrom":[makeQuery(id+"F3.opExtrude","SWEPT_FACE",FACE,{"disambiguationData":[OSD([sQuery(id+"F2.wireOp",EDGE,"E21")])]}),makeQuery(id+"F7.opExtrude","SWEPT_FACE",FACE,{"disambiguationData":[OSD([sQuery(id+"F6.wireOp",EDGE,"E25.top")])]})]}),makeQuery(id+"F3.opExtrude","SWEPT_FACE",FACE,{"disambiguationData":[OSD([sQuery(id+"F2.wireOp",EDGE,"E22.right")])]})],"blendedInto":[makeQuery(id+"F3.opExtrude","SWEPT_FACE",FACE,{"disambiguationData":[OSD([sQuery(id+"F2.wireOp",EDGE,"E22.right")])]})]});
            var Q20;
            Q20=makeQuery(id+"F3.opExtrude","SWEPT_EDGE",EDGE,{"disambiguationData":[OSD([sQuery(id+"F2.wireOp",EDGE,"E20.0"),sQuery(id+"F2.wireOp",EDGE,"E22.right")])]});
            var Q21;
            Q21=makeQuery(id+"F495DjvZ0ecShgZ_1.1.F3.opExtrude","SWEPT_EDGE",EDGE,{"disambiguationData":[OSD([sQuery(id+"F2.wireOp",EDGE,"E20.0"),sQuery(id+"F2.wireOp",EDGE,"E22.right")])]});
            var Q22;
            Q22=makeQuery(id+"F495DjvZ0ecShgZ_1.1.F3.opExtrude","SWEPT_EDGE",EDGE,{"disambiguationData":[OSD([sQuery(id+"F2.wireOp",EDGE,"E20.1"),sQuery(id+"F2.wireOp",EDGE,"E22.top")])]});
            var Q23;
            Q23=makeQuery(id+"F495DjvZ0ecShgZ_1.1.F7.opExtrude","SWEPT_EDGE",EDGE,{"disambiguationData":[OSD([sQuery(id+"F6.wireOp",EDGE,"E25.bottom"),sQuery(id+"F6.wireOp",EDGE,"E25.right")])]});
            var Q24;
            Q24=makeQuery(id+"F8.opFillet","BLEND_EDGE",EDGE,{"blendedFrom":[makeQuery(id+"F495DjvZ0ecShgZ_1.1.F7.opExtrude","SWEPT_EDGE",EDGE,{"disambiguationData":[OSD([sQuery(id+"F2.wireOp",EDGE,"E21"),sQuery(id+"F6.wireOp",EDGE,"E25.right")])]}),makeQuery(id+"F495DjvZ0ecShgZ_1.1.F3.opExtrude","SWEPT_FACE",FACE,{"disambiguationData":[OSD([sQuery(id+"F2.wireOp",EDGE,"E22.top")])]})],"blendedInto":[makeQuery(id+"F495DjvZ0ecShgZ_1.1.F3.opExtrude","SWEPT_FACE",FACE,{"disambiguationData":[OSD([sQuery(id+"F2.wireOp",EDGE,"E22.top")])]})]});
            var Q25;
            Q25=makeQuery(id+"F495DjvZ0ecShgZ_1.1.F7.opExtrude","SWEPT_EDGE",EDGE,{"disambiguationData":[OSD([sQuery(id+"F6.wireOp",EDGE,"E24.46"),sQuery(id+"F6.wireOp",EDGE,"E24.47"),sQuery(id+"F6.wireOp",EDGE,"E25.bottom"),sQuery(id+"F6.wireOp",EDGE,"E25.left")])]});
            var Q26;
            Q26=makeQuery(id+"F495DjvZ0ecShgZ_1.1.F7.opExtrude","SWEPT_EDGE",EDGE,{"disambiguationData":[OSD([sQuery(id+"F6.wireOp",EDGE,"E25.top"),sQuery(id+"F6.wireOp",EDGE,"E25.left")])]});
            var Q27;
            Q27=makeQuery(id+"F8.opFillet","BLEND_EDGE",EDGE,{"blendedFrom":[makeQuery(id+"F495DjvZ0ecShgZ_1.1.F7.boolean.opBoolean","INTERSECT",EDGE,{"derivedFrom":[makeQuery(id+"F495DjvZ0ecShgZ_1.1.F3.opExtrude","SWEPT_FACE",FACE,{"disambiguationData":[OSD([sQuery(id+"F2.wireOp",EDGE,"E21")])]}),makeQuery(id+"F495DjvZ0ecShgZ_1.1.F7.opExtrude","SWEPT_FACE",FACE,{"disambiguationData":[OSD([sQuery(id+"F6.wireOp",EDGE,"E25.top")])]})]}),makeQuery(id+"F495DjvZ0ecShgZ_1.1.F3.opExtrude","SWEPT_FACE",FACE,{"disambiguationData":[OSD([sQuery(id+"F2.wireOp",EDGE,"E22.right")])]})],"blendedInto":[makeQuery(id+"F495DjvZ0ecShgZ_1.1.F3.opExtrude","SWEPT_FACE",FACE,{"disambiguationData":[OSD([sQuery(id+"F2.wireOp",EDGE,"E22.right")])]})]});
            fillet(context, id + "F9", {"entities" : qUnion([Q0, Q1, Q2, Q3, Q4, Q5, Q6, Q7, Q8, Q9, Q10, Q11, Q12, Q13, Q14, Q15, Q16, Q17, Q18, Q19, Q20, Q21, Q22, Q23, Q24, Q25, Q26, Q27]), "radius" : 1 * mm, "tangentPropagation" : true, "allowEdgeOverflow" : false});
        }
        {
            var Q0;
            {var subQ0=sQuery(id+"F0.wireOp",EDGE,"E11.left");Q0=makeQuery(id+"F1.opExtrude","SWEPT_FACE",FACE,{"disambiguationData":[OSD([subQ0]),TDD([makeQuery(id+"F0.imprint","IMPRINT",EDGE,{"disambiguationData":[TD([[makeQuery(id+"F0.imprint","INTERSECT",VERTEX,{"derivedFrom":[subQ0,sQuery(id+"F0.wireOp",EDGE,"E13.top")]}),-1.0]])],"derivedFrom":subQ0})])]});}
            var sketch = newSketch(context, id + "F10", { "sketchPlane" : qUnion([Q0])});
            skLineSegment(sketch, "E26", {"start": v(-14, 18) * mm, "end": v(14, 18) * mm, "construction": true});
            skCircle(sketch, "E27", {"center": v(-14, 18) * mm, "radius": 0.6 * mm});
            skCircle(sketch, "E28", {"center": v(14, 18) * mm, "radius": 0.6 * mm});
            skArc(sketch, "E29", {"start": v(-12, 18) * mm, "mid": v(-14, 20) * mm, "end": v(-16, 18) * mm});
            skLineSegment(sketch, "E30.bottom", {"start": v(-16, 18) * mm, "end": v(-12, 18) * mm});
            skLineSegment(sketch, "E30.top", {"start": v(-16, 0) * mm, "end": v(-12, 0) * mm});
            skLineSegment(sketch, "E30.left", {"start": v(-16, 18) * mm, "end": v(-16, 0) * mm});
            skLineSegment(sketch, "E30.right", {"start": v(-12, 18) * mm, "end": v(-12, 0) * mm});
            skLineSegment(sketch, "E31.MirrorCS", {"start": v(12, 18) * mm, "end": v(12, 0) * mm});
            skArc(sketch, "E32.MirrorCS", {"start": v(12, 18) * mm, "mid": v(14, 20) * mm, "end": v(16, 18) * mm});
            skLineSegment(sketch, "E33.MirrorCS", {"start": v(16, 18) * mm, "end": v(16, 0) * mm});
            skPoint(sketch, "E34", {"position": v(0, 18) * mm});
            skLineSegment(sketch, "E35", {"start": v(12, 0) * mm, "end": v(16, 0) * mm});
            skSolve(sketch);
        }
        {
            var Q0;
            Q0=makeQuery(id+"F10.imprint","IMPRINT",FACE,{"disambiguationData":[TD([[makeQuery(id+"F10.imprint","IMPRINT",EDGE,{"derivedFrom":sQuery(id+"F10.wireOp",EDGE,"E31.MirrorCS")}),1.0]])]});
            var Q1;
            Q1=makeQuery(id+"F10.imprint","IMPRINT",FACE,{"disambiguationData":[TD([[makeQuery(id+"F10.imprint","IMPRINT",EDGE,{"derivedFrom":sQuery(id+"F10.wireOp",EDGE,"E30.top")}),1.0]])]});
            var Q2;
            {var subQ4=sQuery(id+"F10.wireOp",EDGE,"E29");Q2=makeQuery(id+"F10.imprint","IMPRINT",FACE,{"disambiguationData":[TD([[makeQuery(id+"F10.imprint","IMPRINT",EDGE,{"derivedFrom":subQ4}),1.0]])]});}
            extrude(context, id + "F11", {"entities" : qUnion([Q0, Q1, Q2]), "operationType" : NewBodyOperationType.ADD, "oppositeDirection" : true, "depth" : 2 * mm, "offsetDistance" : 25 * mm});
        }
        {
            var Q0;
            {var subQ0=sQuery(id+"F2.wireOp",EDGE,"E21");Q0=makeQuery(id+"F11.boolean.opBoolean","INTERSECT",EDGE,{"derivedFrom":[makeQuery(id+"F3mywzViK7ot0tf_1.1.FbS9UsEZToCQNxt_1.1.F495DjvZ0ecShgZ_1.1.F7.boolean.opBoolean","MERGE",FACE,{"derivedFrom":[makeQuery(id+"F3mywzViK7ot0tf_1.1.FbS9UsEZToCQNxt_1.1.F495DjvZ0ecShgZ_1.1.F3.opExtrude","CAP_FACE",FACE,{"disambiguationData":[OSD([sQuery(id+"F2.wireOp",EDGE,"E20.0"),sQuery(id+"F2.wireOp",EDGE,"E20.1"),subQ0,sQuery(id+"F2.wireOp",EDGE,"E22.top"),sQuery(id+"F2.wireOp",EDGE,"E22.right")])],"isStart":false}),makeQuery(id+"F3mywzViK7ot0tf_1.1.FbS9UsEZToCQNxt_1.1.F495DjvZ0ecShgZ_1.1.F7.opExtrude","CAP_FACE",FACE,{"disambiguationData":[OSD([subQ0,sQuery(id+"F6.wireOp",EDGE,"E24.6"),sQuery(id+"F6.wireOp",EDGE,"E24.35"),sQuery(id+"F6.wireOp",EDGE,"E25.bottom"),sQuery(id+"F6.wireOp",EDGE,"E25.top"),sQuery(id+"F6.wireOp",EDGE,"E25.left"),sQuery(id+"F6.wireOp",EDGE,"E25.right")])],"isStart":true})]}),makeQuery(id+"F11.opExtrude","CAP_FACE",FACE,{"disambiguationData":[OSD([sQuery(id+"F10.wireOp",EDGE,"E27"),sQuery(id+"F10.wireOp",EDGE,"E29"),sQuery(id+"F10.wireOp",EDGE,"E30.top"),sQuery(id+"F10.wireOp",EDGE,"E30.left"),sQuery(id+"F10.wireOp",EDGE,"E30.right")])],"isStart":false})]});}
            var Q1;
            {var subQ0=sQuery(id+"F2.wireOp",EDGE,"E21");Q1=makeQuery(id+"F11.boolean.opBoolean","INTERSECT",EDGE,{"derivedFrom":[makeQuery(id+"F7.boolean.opBoolean","MERGE",FACE,{"derivedFrom":[makeQuery(id+"F3.opExtrude","CAP_FACE",FACE,{"disambiguationData":[OSD([sQuery(id+"F2.wireOp",EDGE,"E20.0"),sQuery(id+"F2.wireOp",EDGE,"E20.1"),subQ0,sQuery(id+"F2.wireOp",EDGE,"E22.top"),sQuery(id+"F2.wireOp",EDGE,"E22.right")])],"isStart":false}),makeQuery(id+"F7.opExtrude","CAP_FACE",FACE,{"disambiguationData":[OSD([subQ0,sQuery(id+"F6.wireOp",EDGE,"E24.6"),sQuery(id+"F6.wireOp",EDGE,"E24.35"),sQuery(id+"F6.wireOp",EDGE,"E25.bottom"),sQuery(id+"F6.wireOp",EDGE,"E25.top"),sQuery(id+"F6.wireOp",EDGE,"E25.left"),sQuery(id+"F6.wireOp",EDGE,"E25.right")])],"isStart":true})]}),makeQuery(id+"F11.opExtrude","CAP_FACE",FACE,{"disambiguationData":[OSD([sQuery(id+"F10.wireOp",EDGE,"E31.MirrorCS"),sQuery(id+"F10.wireOp",EDGE,"E32.MirrorCS"),sQuery(id+"F10.wireOp",EDGE,"E28"),sQuery(id+"F10.wireOp",EDGE,"E33.MirrorCS"),sQuery(id+"F10.wireOp",EDGE,"E35")])],"isStart":false})]});}
            var Q2;
            {var subQ0=sQuery(id+"F2.wireOp",EDGE,"E21");Q2=makeQuery(id+"F11.boolean.opBoolean","INTERSECT",EDGE,{"derivedFrom":[makeQuery(id+"F7.boolean.opBoolean","MERGE",FACE,{"derivedFrom":[makeQuery(id+"F3.opExtrude","CAP_FACE",FACE,{"disambiguationData":[OSD([sQuery(id+"F2.wireOp",EDGE,"E20.0"),sQuery(id+"F2.wireOp",EDGE,"E20.1"),subQ0,sQuery(id+"F2.wireOp",EDGE,"E22.top"),sQuery(id+"F2.wireOp",EDGE,"E22.right")])],"isStart":false}),makeQuery(id+"F7.opExtrude","CAP_FACE",FACE,{"disambiguationData":[OSD([subQ0,sQuery(id+"F6.wireOp",EDGE,"E24.6"),sQuery(id+"F6.wireOp",EDGE,"E24.35"),sQuery(id+"F6.wireOp",EDGE,"E25.bottom"),sQuery(id+"F6.wireOp",EDGE,"E25.top"),sQuery(id+"F6.wireOp",EDGE,"E25.left"),sQuery(id+"F6.wireOp",EDGE,"E25.right")])],"isStart":true})]}),makeQuery(id+"F11.opExtrude","SWEPT_FACE",FACE,{"disambiguationData":[OSD([sQuery(id+"F10.wireOp",EDGE,"E31.MirrorCS")])]})]});}
            var Q3;
            {var subQ0=sQuery(id+"F2.wireOp",EDGE,"E21");Q3=makeQuery(id+"F11.boolean.opBoolean","INTERSECT",EDGE,{"derivedFrom":[makeQuery(id+"F7.boolean.opBoolean","MERGE",FACE,{"derivedFrom":[makeQuery(id+"F3.opExtrude","CAP_FACE",FACE,{"disambiguationData":[OSD([sQuery(id+"F2.wireOp",EDGE,"E20.0"),sQuery(id+"F2.wireOp",EDGE,"E20.1"),subQ0,sQuery(id+"F2.wireOp",EDGE,"E22.top"),sQuery(id+"F2.wireOp",EDGE,"E22.right")])],"isStart":false}),makeQuery(id+"F7.opExtrude","CAP_FACE",FACE,{"disambiguationData":[OSD([subQ0,sQuery(id+"F6.wireOp",EDGE,"E24.6"),sQuery(id+"F6.wireOp",EDGE,"E24.35"),sQuery(id+"F6.wireOp",EDGE,"E25.bottom"),sQuery(id+"F6.wireOp",EDGE,"E25.top"),sQuery(id+"F6.wireOp",EDGE,"E25.left"),sQuery(id+"F6.wireOp",EDGE,"E25.right")])],"isStart":true})]}),makeQuery(id+"F11.opExtrude","SWEPT_FACE",FACE,{"disambiguationData":[OSD([sQuery(id+"F10.wireOp",EDGE,"E33.MirrorCS")])]})]});}
            var Q4;
            {var subQ0=sQuery(id+"F2.wireOp",EDGE,"E21");Q4=makeQuery(id+"F11.boolean.opBoolean","INTERSECT",EDGE,{"derivedFrom":[makeQuery(id+"F3mywzViK7ot0tf_1.1.FbS9UsEZToCQNxt_1.1.F495DjvZ0ecShgZ_1.1.F7.boolean.opBoolean","MERGE",FACE,{"derivedFrom":[makeQuery(id+"F3mywzViK7ot0tf_1.1.FbS9UsEZToCQNxt_1.1.F495DjvZ0ecShgZ_1.1.F3.opExtrude","CAP_FACE",FACE,{"disambiguationData":[OSD([sQuery(id+"F2.wireOp",EDGE,"E20.0"),sQuery(id+"F2.wireOp",EDGE,"E20.1"),subQ0,sQuery(id+"F2.wireOp",EDGE,"E22.top"),sQuery(id+"F2.wireOp",EDGE,"E22.right")])],"isStart":false}),makeQuery(id+"F3mywzViK7ot0tf_1.1.FbS9UsEZToCQNxt_1.1.F495DjvZ0ecShgZ_1.1.F7.opExtrude","CAP_FACE",FACE,{"disambiguationData":[OSD([subQ0,sQuery(id+"F6.wireOp",EDGE,"E24.6"),sQuery(id+"F6.wireOp",EDGE,"E24.35"),sQuery(id+"F6.wireOp",EDGE,"E25.bottom"),sQuery(id+"F6.wireOp",EDGE,"E25.top"),sQuery(id+"F6.wireOp",EDGE,"E25.left"),sQuery(id+"F6.wireOp",EDGE,"E25.right")])],"isStart":true})]}),makeQuery(id+"F11.opExtrude","SWEPT_FACE",FACE,{"disambiguationData":[OSD([sQuery(id+"F10.wireOp",EDGE,"E30.left")])]})]});}
            var Q5;
            {var subQ0=sQuery(id+"F2.wireOp",EDGE,"E21");Q5=makeQuery(id+"F11.boolean.opBoolean","INTERSECT",EDGE,{"derivedFrom":[makeQuery(id+"F3mywzViK7ot0tf_1.1.FbS9UsEZToCQNxt_1.1.F495DjvZ0ecShgZ_1.1.F7.boolean.opBoolean","MERGE",FACE,{"derivedFrom":[makeQuery(id+"F3mywzViK7ot0tf_1.1.FbS9UsEZToCQNxt_1.1.F495DjvZ0ecShgZ_1.1.F3.opExtrude","CAP_FACE",FACE,{"disambiguationData":[OSD([sQuery(id+"F2.wireOp",EDGE,"E20.0"),sQuery(id+"F2.wireOp",EDGE,"E20.1"),subQ0,sQuery(id+"F2.wireOp",EDGE,"E22.top"),sQuery(id+"F2.wireOp",EDGE,"E22.right")])],"isStart":false}),makeQuery(id+"F3mywzViK7ot0tf_1.1.FbS9UsEZToCQNxt_1.1.F495DjvZ0ecShgZ_1.1.F7.opExtrude","CAP_FACE",FACE,{"disambiguationData":[OSD([subQ0,sQuery(id+"F6.wireOp",EDGE,"E24.6"),sQuery(id+"F6.wireOp",EDGE,"E24.35"),sQuery(id+"F6.wireOp",EDGE,"E25.bottom"),sQuery(id+"F6.wireOp",EDGE,"E25.top"),sQuery(id+"F6.wireOp",EDGE,"E25.left"),sQuery(id+"F6.wireOp",EDGE,"E25.right")])],"isStart":true})]}),makeQuery(id+"F11.opExtrude","SWEPT_FACE",FACE,{"disambiguationData":[OSD([sQuery(id+"F10.wireOp",EDGE,"E30.right")])]})]});}
            var Q6;
            {var subQ0=sQuery(id+"F2.wireOp",EDGE,"E21");Q6=makeQuery(id+"FKZCbXvPKaK7P5H_1.1.F11.boolean.opBoolean","INTERSECT",EDGE,{"derivedFrom":[makeQuery(id+"F495DjvZ0ecShgZ_1.1.F7.boolean.opBoolean","MERGE",FACE,{"derivedFrom":[makeQuery(id+"F495DjvZ0ecShgZ_1.1.F3.opExtrude","CAP_FACE",FACE,{"disambiguationData":[OSD([sQuery(id+"F2.wireOp",EDGE,"E20.0"),sQuery(id+"F2.wireOp",EDGE,"E20.1"),subQ0,sQuery(id+"F2.wireOp",EDGE,"E22.top"),sQuery(id+"F2.wireOp",EDGE,"E22.right")])],"isStart":false}),makeQuery(id+"F495DjvZ0ecShgZ_1.1.F7.opExtrude","CAP_FACE",FACE,{"disambiguationData":[OSD([subQ0,sQuery(id+"F6.wireOp",EDGE,"E24.6"),sQuery(id+"F6.wireOp",EDGE,"E24.35"),sQuery(id+"F6.wireOp",EDGE,"E25.bottom"),sQuery(id+"F6.wireOp",EDGE,"E25.top"),sQuery(id+"F6.wireOp",EDGE,"E25.left"),sQuery(id+"F6.wireOp",EDGE,"E25.right")])],"isStart":true})]}),makeQuery(id+"FKZCbXvPKaK7P5H_1.1.F11.opExtrude","CAP_FACE",FACE,{"disambiguationData":[OSD([sQuery(id+"F10.wireOp",EDGE,"E31.MirrorCS"),sQuery(id+"F10.wireOp",EDGE,"E32.MirrorCS"),sQuery(id+"F10.wireOp",EDGE,"E28"),sQuery(id+"F10.wireOp",EDGE,"E33.MirrorCS"),sQuery(id+"F10.wireOp",EDGE,"E35")])],"isStart":false})]});}
            var Q7;
            {var subQ0=sQuery(id+"F2.wireOp",EDGE,"E21");Q7=makeQuery(id+"FKZCbXvPKaK7P5H_1.1.F11.boolean.opBoolean","INTERSECT",EDGE,{"derivedFrom":[makeQuery(id+"F495DjvZ0ecShgZ_1.1.F7.boolean.opBoolean","MERGE",FACE,{"derivedFrom":[makeQuery(id+"F495DjvZ0ecShgZ_1.1.F3.opExtrude","CAP_FACE",FACE,{"disambiguationData":[OSD([sQuery(id+"F2.wireOp",EDGE,"E20.0"),sQuery(id+"F2.wireOp",EDGE,"E20.1"),subQ0,sQuery(id+"F2.wireOp",EDGE,"E22.top"),sQuery(id+"F2.wireOp",EDGE,"E22.right")])],"isStart":false}),makeQuery(id+"F495DjvZ0ecShgZ_1.1.F7.opExtrude","CAP_FACE",FACE,{"disambiguationData":[OSD([subQ0,sQuery(id+"F6.wireOp",EDGE,"E24.6"),sQuery(id+"F6.wireOp",EDGE,"E24.35"),sQuery(id+"F6.wireOp",EDGE,"E25.bottom"),sQuery(id+"F6.wireOp",EDGE,"E25.top"),sQuery(id+"F6.wireOp",EDGE,"E25.left"),sQuery(id+"F6.wireOp",EDGE,"E25.right")])],"isStart":true})]}),makeQuery(id+"FKZCbXvPKaK7P5H_1.1.F11.opExtrude","SWEPT_FACE",FACE,{"disambiguationData":[OSD([sQuery(id+"F10.wireOp",EDGE,"E33.MirrorCS")])]})]});}
            var Q8;
            {var subQ0=sQuery(id+"F2.wireOp",EDGE,"E21");Q8=makeQuery(id+"FKZCbXvPKaK7P5H_1.1.F11.boolean.opBoolean","INTERSECT",EDGE,{"derivedFrom":[makeQuery(id+"F495DjvZ0ecShgZ_1.1.F7.boolean.opBoolean","MERGE",FACE,{"derivedFrom":[makeQuery(id+"F495DjvZ0ecShgZ_1.1.F3.opExtrude","CAP_FACE",FACE,{"disambiguationData":[OSD([sQuery(id+"F2.wireOp",EDGE,"E20.0"),sQuery(id+"F2.wireOp",EDGE,"E20.1"),subQ0,sQuery(id+"F2.wireOp",EDGE,"E22.top"),sQuery(id+"F2.wireOp",EDGE,"E22.right")])],"isStart":false}),makeQuery(id+"F495DjvZ0ecShgZ_1.1.F7.opExtrude","CAP_FACE",FACE,{"disambiguationData":[OSD([subQ0,sQuery(id+"F6.wireOp",EDGE,"E24.6"),sQuery(id+"F6.wireOp",EDGE,"E24.35"),sQuery(id+"F6.wireOp",EDGE,"E25.bottom"),sQuery(id+"F6.wireOp",EDGE,"E25.top"),sQuery(id+"F6.wireOp",EDGE,"E25.left"),sQuery(id+"F6.wireOp",EDGE,"E25.right")])],"isStart":true})]}),makeQuery(id+"FKZCbXvPKaK7P5H_1.1.F11.opExtrude","SWEPT_FACE",FACE,{"disambiguationData":[OSD([sQuery(id+"F10.wireOp",EDGE,"E31.MirrorCS")])]})]});}
            var Q9;
            {var subQ0=sQuery(id+"F2.wireOp",EDGE,"E21");Q9=makeQuery(id+"FKZCbXvPKaK7P5H_1.1.F11.boolean.opBoolean","INTERSECT",EDGE,{"derivedFrom":[makeQuery(id+"FbS9UsEZToCQNxt_1.1.F495DjvZ0ecShgZ_1.1.F7.boolean.opBoolean","MERGE",FACE,{"derivedFrom":[makeQuery(id+"FbS9UsEZToCQNxt_1.1.F495DjvZ0ecShgZ_1.1.F3.opExtrude","CAP_FACE",FACE,{"disambiguationData":[OSD([sQuery(id+"F2.wireOp",EDGE,"E20.0"),sQuery(id+"F2.wireOp",EDGE,"E20.1"),subQ0,sQuery(id+"F2.wireOp",EDGE,"E22.top"),sQuery(id+"F2.wireOp",EDGE,"E22.right")])],"isStart":false}),makeQuery(id+"FbS9UsEZToCQNxt_1.1.F495DjvZ0ecShgZ_1.1.F7.opExtrude","CAP_FACE",FACE,{"disambiguationData":[OSD([subQ0,sQuery(id+"F6.wireOp",EDGE,"E24.6"),sQuery(id+"F6.wireOp",EDGE,"E24.35"),sQuery(id+"F6.wireOp",EDGE,"E25.bottom"),sQuery(id+"F6.wireOp",EDGE,"E25.top"),sQuery(id+"F6.wireOp",EDGE,"E25.left"),sQuery(id+"F6.wireOp",EDGE,"E25.right")])],"isStart":true})]}),makeQuery(id+"FKZCbXvPKaK7P5H_1.1.F11.opExtrude","SWEPT_FACE",FACE,{"disambiguationData":[OSD([sQuery(id+"F10.wireOp",EDGE,"E30.left")])]})]});}
            var Q10;
            {var subQ0=sQuery(id+"F2.wireOp",EDGE,"E21");Q10=makeQuery(id+"FKZCbXvPKaK7P5H_1.1.F11.boolean.opBoolean","INTERSECT",EDGE,{"derivedFrom":[makeQuery(id+"FbS9UsEZToCQNxt_1.1.F495DjvZ0ecShgZ_1.1.F7.boolean.opBoolean","MERGE",FACE,{"derivedFrom":[makeQuery(id+"FbS9UsEZToCQNxt_1.1.F495DjvZ0ecShgZ_1.1.F3.opExtrude","CAP_FACE",FACE,{"disambiguationData":[OSD([sQuery(id+"F2.wireOp",EDGE,"E20.0"),sQuery(id+"F2.wireOp",EDGE,"E20.1"),subQ0,sQuery(id+"F2.wireOp",EDGE,"E22.top"),sQuery(id+"F2.wireOp",EDGE,"E22.right")])],"isStart":false}),makeQuery(id+"FbS9UsEZToCQNxt_1.1.F495DjvZ0ecShgZ_1.1.F7.opExtrude","CAP_FACE",FACE,{"disambiguationData":[OSD([subQ0,sQuery(id+"F6.wireOp",EDGE,"E24.6"),sQuery(id+"F6.wireOp",EDGE,"E24.35"),sQuery(id+"F6.wireOp",EDGE,"E25.bottom"),sQuery(id+"F6.wireOp",EDGE,"E25.top"),sQuery(id+"F6.wireOp",EDGE,"E25.left"),sQuery(id+"F6.wireOp",EDGE,"E25.right")])],"isStart":true})]}),makeQuery(id+"FKZCbXvPKaK7P5H_1.1.F11.opExtrude","CAP_FACE",FACE,{"disambiguationData":[OSD([sQuery(id+"F10.wireOp",EDGE,"E27"),sQuery(id+"F10.wireOp",EDGE,"E29"),sQuery(id+"F10.wireOp",EDGE,"E30.top"),sQuery(id+"F10.wireOp",EDGE,"E30.left"),sQuery(id+"F10.wireOp",EDGE,"E30.right")])],"isStart":false})]});}
            var Q11;
            {var subQ0=sQuery(id+"F2.wireOp",EDGE,"E21");Q11=makeQuery(id+"FKZCbXvPKaK7P5H_1.1.F11.boolean.opBoolean","INTERSECT",EDGE,{"derivedFrom":[makeQuery(id+"FbS9UsEZToCQNxt_1.1.F495DjvZ0ecShgZ_1.1.F7.boolean.opBoolean","MERGE",FACE,{"derivedFrom":[makeQuery(id+"FbS9UsEZToCQNxt_1.1.F495DjvZ0ecShgZ_1.1.F3.opExtrude","CAP_FACE",FACE,{"disambiguationData":[OSD([sQuery(id+"F2.wireOp",EDGE,"E20.0"),sQuery(id+"F2.wireOp",EDGE,"E20.1"),subQ0,sQuery(id+"F2.wireOp",EDGE,"E22.top"),sQuery(id+"F2.wireOp",EDGE,"E22.right")])],"isStart":false}),makeQuery(id+"FbS9UsEZToCQNxt_1.1.F495DjvZ0ecShgZ_1.1.F7.opExtrude","CAP_FACE",FACE,{"disambiguationData":[OSD([subQ0,sQuery(id+"F6.wireOp",EDGE,"E24.6"),sQuery(id+"F6.wireOp",EDGE,"E24.35"),sQuery(id+"F6.wireOp",EDGE,"E25.bottom"),sQuery(id+"F6.wireOp",EDGE,"E25.top"),sQuery(id+"F6.wireOp",EDGE,"E25.left"),sQuery(id+"F6.wireOp",EDGE,"E25.right")])],"isStart":true})]}),makeQuery(id+"FKZCbXvPKaK7P5H_1.1.F11.opExtrude","SWEPT_FACE",FACE,{"disambiguationData":[OSD([sQuery(id+"F10.wireOp",EDGE,"E30.right")])]})]});}
            fillet(context, id + "F12", {"entities" : qUnion([Q0, Q1, Q2, Q3, Q4, Q5, Q6, Q7, Q8, Q9, Q10, Q11]), "radius" : 2 * mm, "tangentPropagation" : true, "allowEdgeOverflow" : false});
        }
    });
